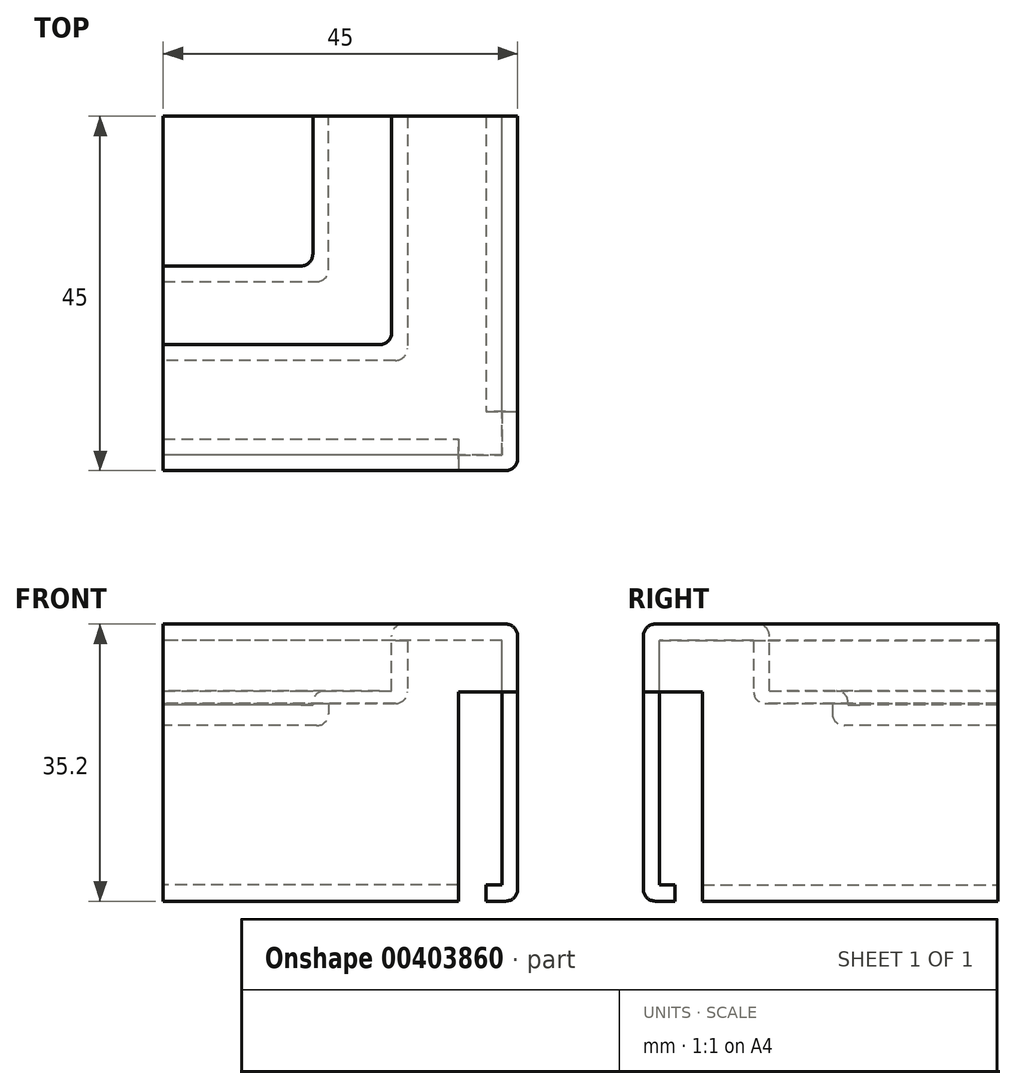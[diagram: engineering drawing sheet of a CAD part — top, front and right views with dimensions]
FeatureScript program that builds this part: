
annotation { "Feature Type Name" : "Feature", "Feature Type Description" : "" }
export const myFeature = defineFeature(function(context is Context, id is Id, definition is map)
    precondition{}
    {
        {
            var Q0;
            Q0=qCreatedBy(makeId("Right.planeOp"),FACE);
            var sketch = newSketch(context, id + "F0", { "sketchPlane" : qUnion([Q0])});
            skLineSegment(sketch, "E0.bottom", {"start": v(22.5, -17.6) * mm, "end": v(-22.5, -17.6) * mm});
            skLineSegment(sketch, "E0.top", {"start": v(22.5, 17.6) * mm, "end": v(-22.5, 17.6) * mm});
            skLineSegment(sketch, "E0.left", {"start": v(22.5, -17.6) * mm, "end": v(22.5, 17.6) * mm});
            skLineSegment(sketch, "E0.right", {"start": v(-22.5, -17.6) * mm, "end": v(-22.5, 17.6) * mm});
            skPoint(sketch, "E0.middle", {"position": v(0, 0) * mm});
            skSolve(sketch);
        }
        {
            var Q0;
            Q0=makeQuery(id+"F0.imprint","IMPRINT",FACE,{"disambiguationData":[TD([[makeQuery(id+"F0.imprint","IMPRINT",EDGE,{"derivedFrom":sQuery(id+"F0.wireOp",EDGE,"E0.bottom")}),-1.0]])]});
            extrude(context, id + "F1", {"entities" : qUnion([Q0]), "depth" : 45 * mm});
        }
        {
            var Q0;
            Q0=qCreatedBy(makeId("Top.planeOp"),FACE);
            var sketch = newSketch(context, id + "F2", { "sketchPlane" : qUnion([Q0])});
            skLineSegment(sketch, "E1.bottom", {"start": v(0, 22.5) * mm, "end": v(29, 22.5) * mm});
            skLineSegment(sketch, "E1.top", {"start": v(0, -6.5) * mm, "end": v(29, -6.5) * mm});
            skLineSegment(sketch, "E1.left", {"start": v(0, 22.5) * mm, "end": v(0, -6.5) * mm});
            skLineSegment(sketch, "E1.right", {"start": v(29, 22.5) * mm, "end": v(29, -6.5) * mm});
            skSolve(sketch);
        }
        {
            var Q0;
            Q0 = qSketchRegion(id + "F2", true);
            extrude(context, id + "F3", {"entities" : qUnion([Q0]), "operationType" : NewBodyOperationType.REMOVE, "endBound" : BoundingType.SYMMETRIC, "oppositeDirection" : true, "depth" : 45 * mm});
        }
        {
            var Q0;
            Q0=qCreatedBy(makeId("Top.planeOp"),FACE);
            var sketch = newSketch(context, id + "F4", { "sketchPlane" : qUnion([Q0])});
            skLineSegment(sketch, "E2.bottom", {"start": v(43, -20.5) * mm, "end": v(-4, -20.5) * mm});
            skLineSegment(sketch, "E2.top", {"start": v(43, 26.5) * mm, "end": v(-4, 26.5) * mm});
            skLineSegment(sketch, "E2.left", {"start": v(43, -20.5) * mm, "end": v(43, 26.5) * mm});
            skLineSegment(sketch, "E2.right", {"start": v(-4, -20.5) * mm, "end": v(-4, 26.5) * mm});
            skSolve(sketch);
        }
        {
            var Q0;
            Q0 = qSketchRegion(id + "F4", true);
            extrude(context, id + "F5", {"entities" : qUnion([Q0]), "operationType" : NewBodyOperationType.REMOVE, "endBound" : BoundingType.SYMMETRIC, "oppositeDirection" : true, "depth" : 31 * mm});
        }
        {
            var Q0;
            Q0=qCreatedBy(makeId("Top.planeOp"),FACE);
            var sketch = newSketch(context, id + "F6", { "sketchPlane" : qUnion([Q0])});
            skLineSegment(sketch, "E3.bottom", {"start": v(41, -18.5) * mm, "end": v(-6, -18.5) * mm});
            skLineSegment(sketch, "E3.top", {"start": v(41, 28.5) * mm, "end": v(-6, 28.5) * mm});
            skLineSegment(sketch, "E3.left", {"start": v(41, -18.5) * mm, "end": v(41, 28.5) * mm});
            skLineSegment(sketch, "E3.right", {"start": v(-6, -18.5) * mm, "end": v(-6, 28.5) * mm});
            skSolve(sketch);
        }
        {
            var Q0;
            Q0=makeQuery(id+"F6.imprint","IMPRINT",FACE,{"disambiguationData":[TD([[makeQuery(id+"F6.imprint","IMPRINT",EDGE,{"derivedFrom":sQuery(id+"F6.wireOp",EDGE,"E3.bottom")}),-1.0]])]});
            extrude(context, id + "F7", {"entities" : qUnion([Q0]), "operationType" : NewBodyOperationType.REMOVE, "oppositeDirection" : true, "depth" : 28 * mm});
        }
        {
            var Q0;
            Q0=qCreatedBy(makeId("Top.planeOp"),FACE);
            var sketch = newSketch(context, id + "F8", { "sketchPlane" : qUnion([Q0])});
            skLineSegment(sketch, "E4.bottom", {"start": v(37.5, -15) * mm, "end": v(52.5, -15) * mm});
            skLineSegment(sketch, "E4.top", {"start": v(37.5, -30) * mm, "end": v(52.5, -30) * mm});
            skLineSegment(sketch, "E4.left", {"start": v(37.5, -15) * mm, "end": v(37.5, -30) * mm});
            skLineSegment(sketch, "E4.right", {"start": v(52.5, -15) * mm, "end": v(52.5, -30) * mm});
            skSolve(sketch);
        }
        {
            var Q0;
            Q0=makeQuery(id+"F8.imprint","IMPRINT",FACE,{"disambiguationData":[TD([[makeQuery(id+"F8.imprint","IMPRINT",EDGE,{"derivedFrom":sQuery(id+"F8.wireOp",EDGE,"E4.bottom")}),-1.0]])]});
            extrude(context, id + "F9", {"entities" : qUnion([Q0]), "operationType" : NewBodyOperationType.REMOVE, "oppositeDirection" : true, "depth" : 24.7 * mm, "hasSecondDirection" : true, "secondDirectionOppositeDirection" : false, "secondDirectionDepth" : 9 * mm});
        }
        {
            var Q0;
            Q0=qCreatedBy(makeId("Top.planeOp"),FACE);
            var sketch = newSketch(context, id + "F10", { "sketchPlane" : qUnion([Q0])});
            skLineSegment(sketch, "E5", {"start": v(29, 22.5) * mm, "end": v(31, 22.5) * mm});
            skLineSegment(sketch, "E6", {"start": v(31, 22.5) * mm, "end": v(31, -8.5) * mm});
            skLineSegment(sketch, "E7", {"start": v(31, -8.5) * mm, "end": v(0, -8.5) * mm});
            skLineSegment(sketch, "E8", {"start": v(0, -8.5) * mm, "end": v(0, -6.5) * mm});
            skLineSegment(sketch, "E9", {"start": v(0, -6.5) * mm, "end": v(29, -6.5) * mm});
            skLineSegment(sketch, "E10", {"start": v(29, -6.5) * mm, "end": v(29, 22.5) * mm});
            skSolve(sketch);
        }
        {
            var Q0;
            Q0=makeQuery(id+"F10.imprint","IMPRINT",FACE,{"disambiguationData":[TD([[makeQuery(id+"F10.imprint","IMPRINT",EDGE,{"derivedFrom":sQuery(id+"F10.wireOp",EDGE,"E5")}),-1.0]])]});
            var Q1;
            Q1=makeQuery(id+"F5.boolean.opBoolean","COPY",FACE,{"derivedFrom":makeQuery(id+"F5.opExtrude","CAP_FACE",FACE,{"disambiguationData":[OSD([sQuery(id+"F4.wireOp",EDGE,"E2.bottom"),sQuery(id+"F4.wireOp",EDGE,"E2.top"),sQuery(id+"F4.wireOp",EDGE,"E2.left"),sQuery(id+"F4.wireOp",EDGE,"E2.right")])],"isStart":true})});
            extrude(context, id + "F11", {"entities" : qUnion([Q0]), "operationType" : NewBodyOperationType.ADD, "endBound" : BoundingType.UP_TO_SURFACE, "endBoundEntityFace" : qUnion([Q1]), "depth" : 17 * mm, "hasSecondDirection" : true, "secondDirectionOppositeDirection" : false, "secondDirectionDepth" : 7.5 * mm});
        }
        {
            var Q0;
            Q0=qCreatedBy(makeId("Top.planeOp"),FACE);
            var sketch = newSketch(context, id + "F12", { "sketchPlane" : qUnion([Q0])});
            skLineSegment(sketch, "E11", {"start": v(29, 22.5) * mm, "end": v(29, -6.5) * mm});
            skLineSegment(sketch, "E12", {"start": v(29, -6.5) * mm, "end": v(0, -6.5) * mm});
            skLineSegment(sketch, "E13", {"start": v(0, -6.5) * mm, "end": v(0, 3.5) * mm});
            skLineSegment(sketch, "E14", {"start": v(0, 3.5) * mm, "end": v(19, 3.5) * mm});
            skLineSegment(sketch, "E15", {"start": v(19, 3.5) * mm, "end": v(19, 22.5) * mm});
            skLineSegment(sketch, "E16", {"start": v(19, 22.5) * mm, "end": v(29, 22.5) * mm});
            skSolve(sketch);
        }
        {
            var Q0;
            Q0=makeQuery(id+"F12.imprint","IMPRINT",FACE,{"disambiguationData":[TD([[makeQuery(id+"F12.imprint","IMPRINT",EDGE,{"derivedFrom":sQuery(id+"F12.wireOp",EDGE,"E11")}),-1.0]])]});
            extrude(context, id + "F13", {"entities" : qUnion([Q0]), "operationType" : NewBodyOperationType.ADD, "depth" : 9.1 * mm, "hasSecondDirection" : true, "secondDirectionOppositeDirection" : false, "secondDirectionDepth" : 7.5 * mm});
        }
        {
            var Q0;
            Q0=qCreatedBy(makeId("Top.planeOp"),FACE);
            var sketch = newSketch(context, id + "F14", { "sketchPlane" : qUnion([Q0])});
            skLineSegment(sketch, "E17", {"start": v(19, 22.5) * mm, "end": v(19, 3.5) * mm});
            skLineSegment(sketch, "E18", {"start": v(19, 3.5) * mm, "end": v(0, 3.5) * mm});
            skLineSegment(sketch, "E19", {"start": v(0, 3.5) * mm, "end": v(0, 1.5) * mm});
            skLineSegment(sketch, "E20", {"start": v(0, 1.5) * mm, "end": v(21, 1.5) * mm});
            skLineSegment(sketch, "E21", {"start": v(21, 1.5) * mm, "end": v(21, 22.5) * mm});
            skLineSegment(sketch, "E22", {"start": v(21, 22.5) * mm, "end": v(19, 22.5) * mm});
            skSolve(sketch);
        }
        {
            var Q0;
            Q0=makeQuery(id+"F14.imprint","IMPRINT",FACE,{"disambiguationData":[TD([[makeQuery(id+"F14.imprint","IMPRINT",EDGE,{"derivedFrom":sQuery(id+"F14.wireOp",EDGE,"E17")}),1.0]])]});
            var Q1;
            Q1=makeQuery(id+"F13.boolean.opBoolean","MERGE",FACE,{"derivedFrom":[makeQuery(id+"F11.opExtrude","CAP_FACE",FACE,{"disambiguationData":[OSD([sQuery(id+"F10.wireOp",EDGE,"E5"),sQuery(id+"F10.wireOp",EDGE,"E6"),sQuery(id+"F10.wireOp",EDGE,"E7"),sQuery(id+"F10.wireOp",EDGE,"E8"),sQuery(id+"F10.wireOp",EDGE,"E9"),sQuery(id+"F10.wireOp",EDGE,"E10")])],"isStart":true}),makeQuery(id+"F13.opExtrude","CAP_FACE",FACE,{"disambiguationData":[OSD([sQuery(id+"F12.wireOp",EDGE,"E11"),sQuery(id+"F12.wireOp",EDGE,"E12"),sQuery(id+"F12.wireOp",EDGE,"E13"),sQuery(id+"F12.wireOp",EDGE,"E14"),sQuery(id+"F12.wireOp",EDGE,"E15"),sQuery(id+"F12.wireOp",EDGE,"E16")])],"isStart":true})]});
            extrude(context, id + "F15", {"entities" : qUnion([Q0]), "operationType" : NewBodyOperationType.ADD, "endBound" : BoundingType.UP_TO_SURFACE, "endBoundEntityFace" : qUnion([Q1]), "depth" : 25 * mm, "hasSecondDirection" : true, "secondDirectionOppositeDirection" : false, "secondDirectionDepth" : 4.7 * mm});
        }
        {
            var Q0;
            Q0=qCreatedBy(makeId("Top.planeOp"),FACE);
            var sketch = newSketch(context, id + "F16", { "sketchPlane" : qUnion([Q0])});
            skLineSegment(sketch, "E23.bottom", {"start": v(19, 22.5) * mm, "end": v(0, 22.5) * mm});
            skLineSegment(sketch, "E23.top", {"start": v(19, 3.5) * mm, "end": v(0, 3.5) * mm});
            skLineSegment(sketch, "E23.left", {"start": v(19, 22.5) * mm, "end": v(19, 3.5) * mm});
            skLineSegment(sketch, "E23.right", {"start": v(0, 22.5) * mm, "end": v(0, 3.5) * mm});
            skSolve(sketch);
        }
        {
            var Q0;
            Q0=makeQuery(id+"F16.imprint","IMPRINT",FACE,{"disambiguationData":[TD([[makeQuery(id+"F16.imprint","IMPRINT",EDGE,{"derivedFrom":sQuery(id+"F16.wireOp",EDGE,"E23.bottom")}),1.0]])]});
            var Q1;
            Q1=makeQuery(id+"F13.opExtrude","CAP_FACE",FACE,{"disambiguationData":[OSD([sQuery(id+"F12.wireOp",EDGE,"E11"),sQuery(id+"F12.wireOp",EDGE,"E12"),sQuery(id+"F12.wireOp",EDGE,"E13"),sQuery(id+"F12.wireOp",EDGE,"E14"),sQuery(id+"F12.wireOp",EDGE,"E15"),sQuery(id+"F12.wireOp",EDGE,"E16")])],"isStart":false});
            var Q2;
            Q2=makeQuery(id+"F15.opExtrude","CAP_FACE",FACE,{"disambiguationData":[OSD([sQuery(id+"F14.wireOp",EDGE,"E17"),sQuery(id+"F14.wireOp",EDGE,"E18"),sQuery(id+"F14.wireOp",EDGE,"E19"),sQuery(id+"F14.wireOp",EDGE,"E20"),sQuery(id+"F14.wireOp",EDGE,"E21"),sQuery(id+"F14.wireOp",EDGE,"E22")])],"isStart":true});
            extrude(context, id + "F17", {"entities" : qUnion([Q0]), "operationType" : NewBodyOperationType.ADD, "endBoundEntityFace" : qUnion([Q1]), "depth" : 7.3 * mm, "hasSecondDirection" : true, "secondDirectionOppositeDirection" : false, "secondDirectionBoundEntityFace" : qUnion([Q2]), "secondDirectionDepth" : 4.7 * mm});
        }
        {
            var Q0;
            Q0=makeQuery(id+"F1.opExtrude","SWEPT_EDGE",EDGE,{"disambiguationData":[OSD([sQuery(id+"F0.wireOp",EDGE,"E0.top"),sQuery(id+"F0.wireOp",EDGE,"E0.right")])]});
            var Q1;
            Q1=makeQuery(id+"F1.opExtrude","CAP_EDGE",EDGE,{"disambiguationData":[OSD([sQuery(id+"F0.wireOp",EDGE,"E0.top")])],"isStart":false});
            var Q2;
            Q2=makeQuery(id+"F1.opExtrude","CAP_EDGE",EDGE,{"disambiguationData":[OSD([sQuery(id+"F0.wireOp",EDGE,"E0.bottom")])],"isStart":false});
            var Q3;
            Q3=makeQuery(id+"F1.opExtrude","SWEPT_EDGE",EDGE,{"disambiguationData":[OSD([sQuery(id+"F0.wireOp",EDGE,"E0.bottom"),sQuery(id+"F0.wireOp",EDGE,"E0.right")])]});
            var Q4;
            Q4=makeQuery(id+"F3.boolean.opBoolean","INTERSECT",EDGE,{"derivedFrom":[makeQuery(id+"F1.opExtrude","SWEPT_FACE",FACE,{"disambiguationData":[OSD([sQuery(id+"F0.wireOp",EDGE,"E0.top")])]}),makeQuery(id+"F3.opExtrude","SWEPT_FACE",FACE,{"disambiguationData":[OSD([sQuery(id+"F2.wireOp",EDGE,"E1.top")])]})]});
            var Q5;
            Q5=makeQuery(id+"F3.boolean.opBoolean","INTERSECT",EDGE,{"derivedFrom":[makeQuery(id+"F1.opExtrude","SWEPT_FACE",FACE,{"disambiguationData":[OSD([sQuery(id+"F0.wireOp",EDGE,"E0.top")])]}),makeQuery(id+"F3.opExtrude","SWEPT_FACE",FACE,{"disambiguationData":[OSD([sQuery(id+"F2.wireOp",EDGE,"E1.right")])]})]});
            var Q6;
            {var subQ0=sQuery(id+"F2.wireOp",EDGE,"E1.top");var subQ1=sQuery(id+"F2.wireOp",EDGE,"E1.right");Q6=makeQuery(id+"F11.boolean.opBoolean","MERGE",EDGE,{"derivedFrom":[makeQuery(id+"F5.boolean.opBoolean","SPLIT",EDGE,{"disambiguationData":[TD([makeQuery(id+"F1.opExtrude","SWEPT_FACE",FACE,{"disambiguationData":[OSD([sQuery(id+"F0.wireOp",EDGE,"E0.top")])]})])],"derivedFrom":makeQuery(id+"F3.boolean.opBoolean","COPY",EDGE,{"derivedFrom":makeQuery(id+"F3.opExtrude","SWEPT_EDGE",EDGE,{"disambiguationData":[OSD([subQ0,subQ1])]})})}),makeQuery(id+"F11.opExtrude","SWEPT_EDGE",EDGE,{"disambiguationData":[OSD([sQuery(id+"F10.wireOp",EDGE,"E9"),sQuery(id+"F10.wireOp",EDGE,"E10")])]})]});}
            var Q7;
            Q7=makeQuery(id+"F1.opExtrude","CAP_EDGE",EDGE,{"disambiguationData":[OSD([sQuery(id+"F0.wireOp",EDGE,"E0.right")])],"isStart":false});
            var Q8;
            Q8=makeQuery(id+"F13.opExtrude","CAP_EDGE",EDGE,{"disambiguationData":[OSD([sQuery(id+"F12.wireOp",EDGE,"E11")])],"isStart":false});
            var Q9;
            Q9=makeQuery(id+"F13.opExtrude","CAP_EDGE",EDGE,{"disambiguationData":[OSD([sQuery(id+"F12.wireOp",EDGE,"E12")])],"isStart":false});
            var Q10;
            Q10=makeQuery(id+"F13.opExtrude","CAP_EDGE",EDGE,{"disambiguationData":[OSD([sQuery(id+"F12.wireOp",EDGE,"E15")])],"isStart":false});
            var Q11;
            Q11=makeQuery(id+"F13.opExtrude","CAP_EDGE",EDGE,{"disambiguationData":[OSD([sQuery(id+"F12.wireOp",EDGE,"E14")])],"isStart":false});
            var Q12;
            Q12=makeQuery(id+"F15.boolean.opBoolean","MERGE",EDGE,{"derivedFrom":[makeQuery(id+"F13.opExtrude","SWEPT_EDGE",EDGE,{"disambiguationData":[OSD([sQuery(id+"F12.wireOp",EDGE,"E14"),sQuery(id+"F12.wireOp",EDGE,"E15")])]}),makeQuery(id+"F15.opExtrude","SWEPT_EDGE",EDGE,{"disambiguationData":[OSD([sQuery(id+"F14.wireOp",EDGE,"E17"),sQuery(id+"F14.wireOp",EDGE,"E18")])]})]});
            var Q13;
            Q13=makeQuery(id+"F11.opExtrude","CAP_EDGE",EDGE,{"disambiguationData":[OSD([sQuery(id+"F10.wireOp",EDGE,"E6")])],"isStart":true});
            var Q14;
            Q14=makeQuery(id+"F15.opExtrude","CAP_EDGE",EDGE,{"disambiguationData":[OSD([sQuery(id+"F14.wireOp",EDGE,"E21")])],"isStart":true});
            var Q15;
            Q15=makeQuery(id+"F15.opExtrude","CAP_EDGE",EDGE,{"disambiguationData":[OSD([sQuery(id+"F14.wireOp",EDGE,"E20")])],"isStart":true});
            var Q16;
            Q16=makeQuery(id+"F11.opExtrude","CAP_EDGE",EDGE,{"disambiguationData":[OSD([sQuery(id+"F10.wireOp",EDGE,"E7")])],"isStart":true});
            var Q17;
            Q17=makeQuery(id+"F15.opExtrude","SWEPT_EDGE",EDGE,{"disambiguationData":[OSD([sQuery(id+"F14.wireOp",EDGE,"E20"),sQuery(id+"F14.wireOp",EDGE,"E21")])]});
            var Q18;
            Q18=makeQuery(id+"F11.opExtrude","SWEPT_EDGE",EDGE,{"disambiguationData":[OSD([sQuery(id+"F10.wireOp",EDGE,"E6"),sQuery(id+"F10.wireOp",EDGE,"E7")])]});
            fillet(context, id + "F18", {"entities" : qUnion([Q0, Q1, Q2, Q3, Q4, Q5, Q6, Q7, Q8, Q9, Q10, Q11, Q12, Q13, Q14, Q15, Q16, Q17, Q18]), "radius" : 1.5 * mm, "tangentPropagation" : true, "allowEdgeOverflow" : false});
        }
    });
